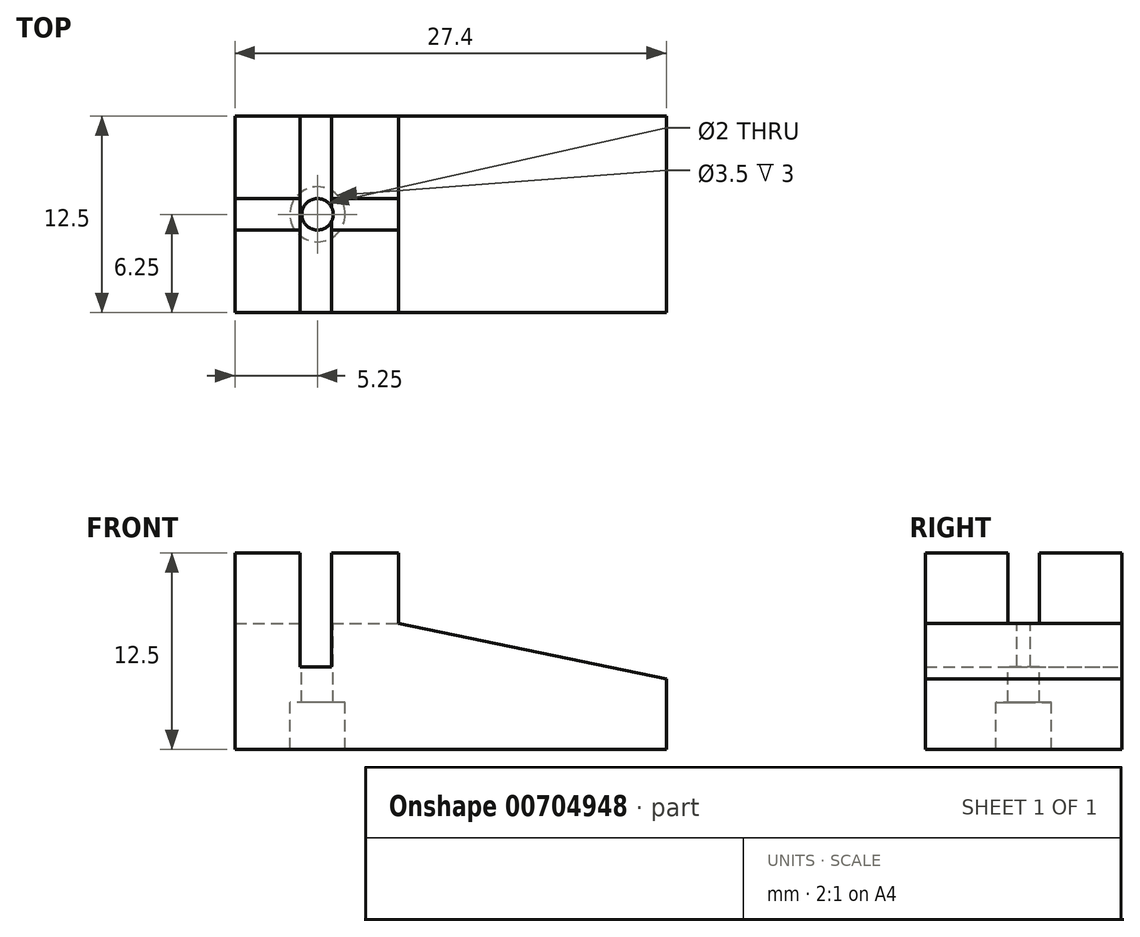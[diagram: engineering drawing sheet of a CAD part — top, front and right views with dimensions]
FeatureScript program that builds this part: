
annotation { "Feature Type Name" : "Feature", "Feature Type Description" : "" }
export const myFeature = defineFeature(function(context is Context, id is Id, definition is map)
    precondition{}
    {
        {
            var Q0;
            Q0=qCreatedBy(makeId("Front.planeOp"),FACE);
            var sketch = newSketch(context, id + "F0", { "sketchPlane" : qUnion([Q0])});
            skLineSegment(sketch, "E0", {"start": v(0, 0) * mm, "end": v(0, 4.5) * mm});
            skLineSegment(sketch, "E1", {"start": v(-10.4, 4.5) * mm, "end": v(-10.4, -8) * mm});
            skLineSegment(sketch, "E2", {"start": v(-10.4, -8) * mm, "end": v(17, -8) * mm});
            skLineSegment(sketch, "E3", {"start": v(17, -8) * mm, "end": v(17, -3.5) * mm});
            skLineSegment(sketch, "E4", {"start": v(17, -3.5) * mm, "end": v(0, 0) * mm});
            skLineSegment(sketch, "E5", {"start": v(0, 4.5) * mm, "end": v(-4.25, 4.5) * mm});
            skLineSegment(sketch, "E6", {"start": v(-6.25, -2.75) * mm, "end": v(-6.25, 4.5) * mm});
            skLineSegment(sketch, "E7", {"start": v(-6.25, 4.5) * mm, "end": v(-10.4, 4.5) * mm});
            skLineSegment(sketch, "E8", {"start": v(-6.25, -2.75) * mm, "end": v(-4.25, -2.75) * mm});
            skLineSegment(sketch, "E9", {"start": v(-4.25, -2.75) * mm, "end": v(-4.25, 4.5) * mm});
            skPoint(sketch, "E10", {"position": v(-5.25, -2.75) * mm});
            skSolve(sketch);
        }
        {
            var Q0;
            Q0=makeQuery(id+"F0.imprint","IMPRINT",FACE,{"disambiguationData":[TD([[makeQuery(id+"F0.imprint","IMPRINT",EDGE,{"derivedFrom":sQuery(id+"F0.wireOp",EDGE,"E0")}),1.0]])]});
            extrude(context, id + "F1", {"entities" : qUnion([Q0]), "depth" : 12.5 * mm, "offsetDistance" : 25 * mm, "symmetric" : true});
        }
        {
            var Q0;
            Q0=qCreatedBy(makeId("Right.planeOp"),FACE);
            var sketch = newSketch(context, id + "F2", { "sketchPlane" : qUnion([Q0])});
            skLineSegment(sketch, "E11.bottom", {"start": v(1, 0) * mm, "end": v(-1, 0) * mm});
            skLineSegment(sketch, "E11.top", {"start": v(1, 4.5) * mm, "end": v(-1, 4.5) * mm});
            skLineSegment(sketch, "E11.left", {"start": v(1, 0) * mm, "end": v(1, 4.5) * mm});
            skLineSegment(sketch, "E11.right", {"start": v(-1, 0) * mm, "end": v(-1, 4.5) * mm});
            skPoint(sketch, "E11.middle", {"position": v(0, 2.25) * mm});
            skSolve(sketch);
        }
        {
            var Q0;
            Q0=makeQuery(id+"F2.imprint","IMPRINT",FACE,{"disambiguationData":[TD([[makeQuery(id+"F2.imprint","IMPRINT",EDGE,{"derivedFrom":sQuery(id+"F2.wireOp",EDGE,"E11.bottom")}),-1.0]])]});
            extrude(context, id + "F3", {"entities" : qUnion([Q0]), "operationType" : NewBodyOperationType.REMOVE, "endBound" : BoundingType.THROUGH_ALL, "oppositeDirection" : true, "depth" : 25 * mm, "offsetDistance" : 25 * mm});
        }
        {
            var Q0;
            Q0=makeQuery(id+"F1.opExtrude","SWEPT_FACE",FACE,{"disambiguationData":[OSD([sQuery(id+"F0.wireOp",EDGE,"E2")])]});
            var sketch = newSketch(context, id + "F4", { "sketchPlane" : qUnion([Q0])});
            skPoint(sketch, "E12", {"position": v(-5.15, 0) * mm});
            skSolve(sketch);
        }
        {
            var Q0;
            Q0=sQuery(id+"F4.wireOp",VERTEX,"E12");
            var Q1;
            Q1=makeQuery(id+"F1.opExtrude","SWEPT_BODY",BODY,{"disambiguationData":[OSD([sQuery(id+"F0.wireOp",EDGE,"E0"),sQuery(id+"F0.wireOp",EDGE,"E1"),sQuery(id+"F0.wireOp",EDGE,"E2"),sQuery(id+"F0.wireOp",EDGE,"E3"),sQuery(id+"F0.wireOp",EDGE,"E4"),sQuery(id+"F0.wireOp",EDGE,"E5"),sQuery(id+"F0.wireOp",EDGE,"E6"),sQuery(id+"F0.wireOp",EDGE,"E7"),sQuery(id+"F0.wireOp",EDGE,"E8"),sQuery(id+"F0.wireOp",EDGE,"E9")])]});
            hole(context, id + "F5", {"style" : HoleStyle.C_BORE, "endStyle" : HoleEndStyle.BLIND, "holeDiameter" : 2 * mm, "cBoreDiameter" : 3.5 * mm, "cBoreDepth" : 3 * mm, "majorDiameter" : 5 * mm, "holeDepth" : 38 * mm, "isTappedThrough" : true, "tappedDepth" : 12 * mm, "tapClearance" : 3, "locations" : qUnion([Q0]), "scope" : qUnion([Q1]), "startStyle" : HoleStartStyle.PART});
        }
    });
